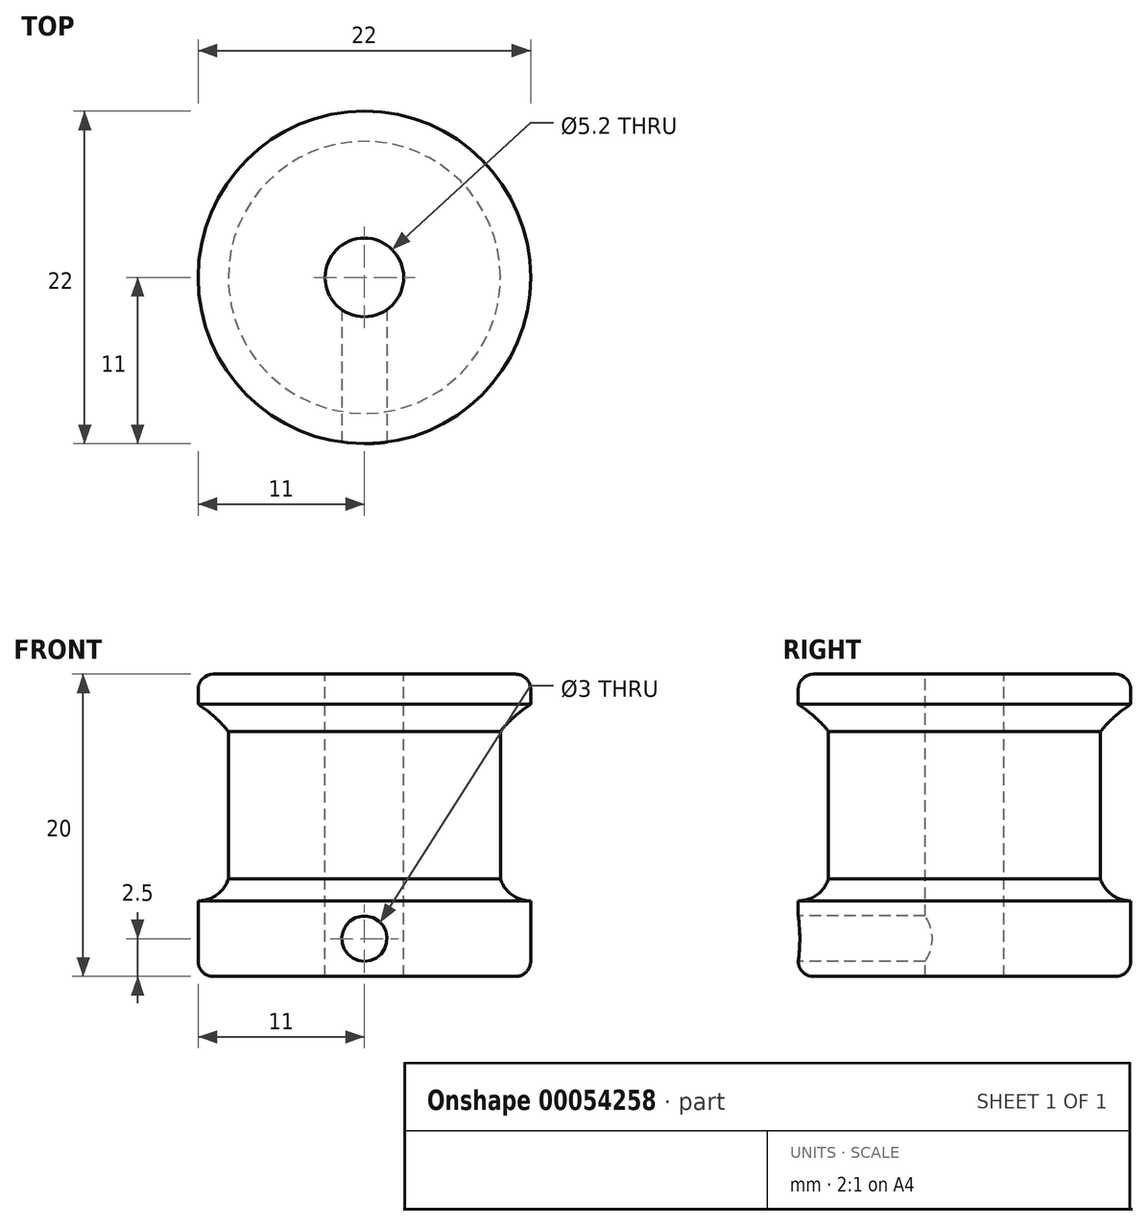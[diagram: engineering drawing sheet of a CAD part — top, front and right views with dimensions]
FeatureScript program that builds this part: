
annotation { "Feature Type Name" : "Feature", "Feature Type Description" : "" }
export const myFeature = defineFeature(function(context is Context, id is Id, definition is map)
    precondition{}
    {
        {
            var Q0;
            Q0=qCreatedBy(makeId("Front.planeOp"),FACE);
            var sketch = newSketch(context, id + "F0", { "sketchPlane" : qUnion([Q0])});
            skLineSegment(sketch, "E0", {"start": v(0, 0) * mm, "end": v(-20.93, 0) * mm});
            skLineSegment(sketch, "E1", {"start": v(0, 20) * mm, "end": v(0, 0) * mm, "construction": true});
            skLineSegment(sketch, "E2.0", {"start": v(0, 20) * mm, "end": v(-20.93, 20) * mm});
            skPoint(sketch, "E3.orphan", {"position": v(0, 67) * mm});
            skLineSegment(sketch, "E4.0", {"start": v(-9, 18) * mm, "end": v(-9, 5) * mm, "construction": true});
            skLineSegment(sketch, "E5.0", {"start": v(-11, 20) * mm, "end": v(-11, 18) * mm, "construction": true});
            skLineSegment(sketch, "E6", {"start": v(-11, 0) * mm, "end": v(0, 0) * mm, "construction": true});
            skLineSegment(sketch, "E7.0", {"start": v(0, 5) * mm, "end": v(-20.93, 5) * mm, "construction": true});
            skLineSegment(sketch, "E8.0", {"start": v(0, 25) * mm, "end": v(-20.93, 25) * mm, "construction": true});
            skLineSegment(sketch, "E9.0", {"start": v(-9, 18) * mm, "end": v(-20.93, 18) * mm});
            skLineSegment(sketch, "E10", {"start": v(-11, 0) * mm, "end": v(-11, 5) * mm});
            skLineSegment(sketch, "E11.trimOffspring", {"start": v(-11, 5) * mm, "end": v(-11, 0) * mm, "construction": true});
            skLineSegment(sketch, "E12", {"start": v(-11, 20) * mm, "end": v(-11, 18) * mm});
            skArc(sketch, "E13", {"start": v(-9, 16.22) * mm, "mid": v(-9.93, 17.19) * mm, "end": v(-11, 18) * mm});
            skArc(sketch, "E14", {"start": v(-11, 5) * mm, "mid": v(-9.76, 5.4) * mm, "end": v(-9, 6.45) * mm});
            skLineSegment(sketch, "E15", {"start": v(-9, 16.22) * mm, "end": v(-9, 6.45) * mm});
            skLineSegment(sketch, "E16", {"start": v(0, 20) * mm, "end": v(0, 0) * mm});
            skSolve(sketch);
        }
        {
            var Q0;
            {var subQ1=sQuery(id+"F0.wireOp",EDGE,"E10");Q0=makeQuery(id+"F0.imprint","IMPRINT",FACE,{"disambiguationData":[TD([[makeQuery(id+"F0.imprint","IMPRINT",EDGE,{"derivedFrom":subQ1}),-1.0]])]});}
            var Q1;
            Q1=sQuery(id+"F0.wireOp",EDGE,"E16");
            revolve(context, id + "F1", {"entities" : qUnion([Q0]), "axis" : qUnion([Q1]), "revolveType" : RevolveType.FULL});
        }
        {
            var Q0;
            Q0=makeQuery(id+"F1.opRevolve","SWEPT_FACE",FACE,{"disambiguationData":[OSD([sQuery(id+"F0.wireOp",EDGE,"E2.0")])]});
            var sketch = newSketch(context, id + "F2", { "sketchPlane" : qUnion([Q0])});
            skPoint(sketch, "E17.0", {"position": v(0, 0) * mm});
            skCircle(sketch, "E18", {"center": v(0, 0) * mm, "radius": 2.6 * mm});
            skSolve(sketch);
        }
        {
            var Q0;
            Q0=makeQuery(id+"F2.imprint","IMPRINT",FACE,{"disambiguationData":[TD([[makeQuery(id+"F2.imprint","IMPRINT",EDGE,{"derivedFrom":sQuery(id+"F2.wireOp",EDGE,"E18")}),1.0]])]});
            extrude(context, id + "F3", {"entities" : qUnion([Q0]), "operationType" : NewBodyOperationType.REMOVE, "oppositeDirection" : true, "depth" : 20 * mm});
        }
        {
            var Q0;
            Q0=qCreatedBy(makeId("Front.planeOp"),FACE);
            cPlane(context, id + "F4", {"entities" : qUnion([Q0]), "cplaneType" : CPlaneType.OFFSET, "offset" : 11 * mm, "width" : 150 * mm, "height" : 150 * mm});
        }
        {
            var Q0;
            Q0=qCreatedBy(id+"F4.planeOp",FACE);
            var sketch = newSketch(context, id + "F5", { "sketchPlane" : qUnion([Q0])});
            skLineSegment(sketch, "E19.0", {"start": v(-11, 0) * mm, "end": v(11, 0) * mm});
            skLineSegment(sketch, "E20.0", {"start": v(-11, 5) * mm, "end": v(11, 5) * mm});
            skLineSegment(sketch, "E21", {"start": v(0, 0) * mm, "end": v(0, 5) * mm, "construction": true});
            skCircle(sketch, "E22", {"center": v(0, 2.5) * mm, "radius": 1.5 * mm});
            skSolve(sketch);
        }
        {
            var Q0;
            Q0=makeQuery(id+"F5.imprint","IMPRINT",FACE,{"disambiguationData":[TD([[makeQuery(id+"F5.imprint","IMPRINT",EDGE,{"derivedFrom":sQuery(id+"F5.wireOp",EDGE,"E22")}),1.0]])]});
            extrude(context, id + "F6", {"entities" : qUnion([Q0]), "operationType" : NewBodyOperationType.REMOVE, "oppositeDirection" : true, "depth" : 10 * mm});
        }
        {
            var Q0;
            Q0=makeQuery(id+"F1.opRevolve","SWEPT_EDGE",EDGE,{"disambiguationData":[OSD([sQuery(id+"F0.wireOp",EDGE,"E2.0"),sQuery(id+"F0.wireOp",EDGE,"E12")])]});
            var Q1;
            Q1=makeQuery(id+"F1.opRevolve","SWEPT_EDGE",EDGE,{"disambiguationData":[OSD([sQuery(id+"F0.wireOp",EDGE,"E0"),sQuery(id+"F0.wireOp",EDGE,"E10")])]});
            fillet(context, id + "F7", {"entities" : qUnion([Q0, Q1]), "radius" : 1 * mm, "tangentPropagation" : true, "allowEdgeOverflow" : false});
        }
    });
